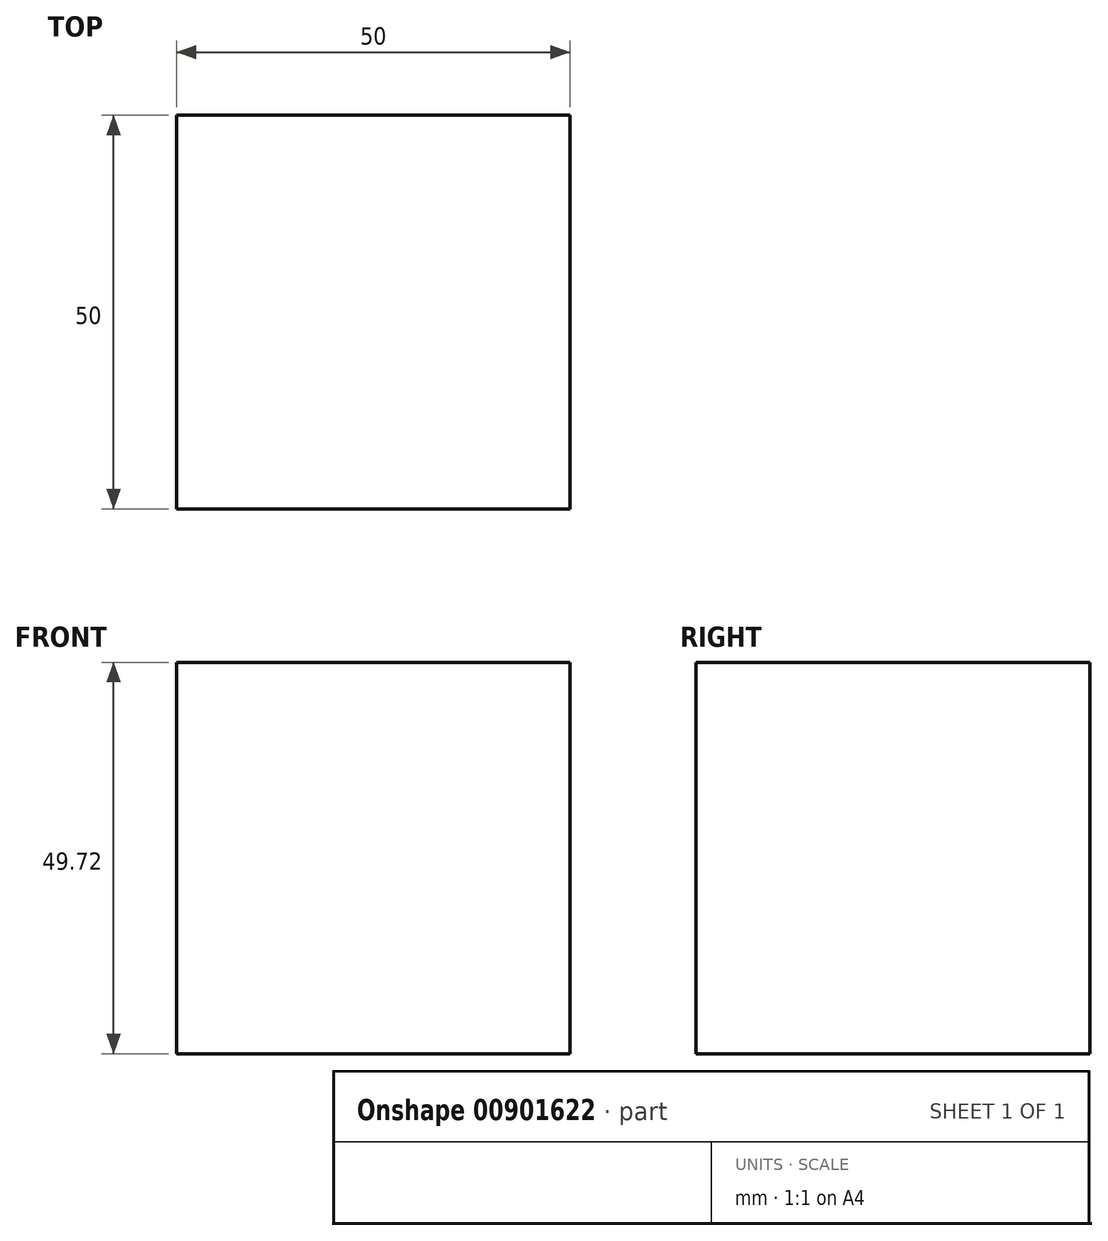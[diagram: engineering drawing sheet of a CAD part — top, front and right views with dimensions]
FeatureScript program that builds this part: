
annotation { "Feature Type Name" : "Feature", "Feature Type Description" : "" }
export const myFeature = defineFeature(function(context is Context, id is Id, definition is map)
    precondition{}
    {
        {
            var Q0;
            Q0=qCreatedBy(makeId("Front.planeOp"),FACE);
            var sketch = newSketch(context, id + "F0", { "sketchPlane" : qUnion([Q0])});
            skLineSegment(sketch, "E0.bottom", {"start": v(-25, 24.86) * mm, "end": v(25, 24.86) * mm});
            skLineSegment(sketch, "E0.top", {"start": v(-25, -24.86) * mm, "end": v(25, -24.86) * mm});
            skLineSegment(sketch, "E0.left", {"start": v(-25, 24.86) * mm, "end": v(-25, -24.86) * mm});
            skLineSegment(sketch, "E0.right", {"start": v(25, 24.86) * mm, "end": v(25, -24.86) * mm});
            skPoint(sketch, "E0.middle", {"position": v(0, 0) * mm});
            skSolve(sketch);
        }
        {
            var Q0;
            Q0 = qSketchRegion(id + "F0", true);
            extrude(context, id + "F1", {"entities" : qUnion([Q0]), "endBound" : BoundingType.SYMMETRIC, "oppositeDirection" : true, "depth" : 50 * mm, "offsetDistance" : 25 * mm});
        }
    });
